# Revit family: NBS_DudleyIndustriesLimited_HndDriers_PlatinumRangeHandDryer
name_source: partatom
category: Specialty Equipment
revit_build: Autodesk Revit 2018 (Build: 20190510_1515(x64)
units: mm (PartAtom-declared; Revit-internal decimal feet)

## family parameters
Cut with Voids When Loaded = No
Host = Face
Part Type = Normal
Room Calculation Point = No
Round Connector Dimension = Use Diameter
Shared = No

## types (1)
- PlatinumRangeHandDryer
    ApparentLoad = 0 VA
    AssetType = Fixed
    BIMObjectName = NBS_DudleyIndustriesLimited_HandDryers_PlatinumRangeHandDryer
    BodyDimensions = 220 x 340 x 170 mm
    BodyFinish = Brushed with clear lacquer
    BodyMaterial = Stainless steel
    Category = Pr_40_70_62_37:Hand dryers
    CodePerformance = CE approved
    Default Elevation = 1300 mm  [stored 4.26509 ft]
    Depth = 0 mm  [stored 0 ft]
    Description = Platinum range hand dryer
    DurationUnit = year
    ElectricalSupplyPowerRating = 1.7 kW
    Features = High performance, robust and reliable, comfortable and quick
    Finish = Brushed with clear lacquer
    HandDryerMaterial = NBS_DudleyIndustriesLimited_StainlessSteel_Brushed
    HasProtectiveEarth = No
    IfcExportAs = IfcElectricApplianceType
    IfcExportType = HANDDRYER
    LoadClassification = Other
    ManufacturerName = Dudley Industries Limited
    ManufacturerURL = www.dudleyindustries.com
    Material = Stainless steel
    ModelNumber = 38155CB
    ModelReference = PlatinumRangeHandDryer
    NBSCertification = www.nationalbimlibrary.com/cert/3l0v0uwc
    NBSDescription = Hand dryers
    NBSReference = 45-35-72/334
    Name = HandDryers_PlatinumRangeHandDryer_DudleyIndustriesLimited
    NominalHeight = 340 mm
    NominalLength = 0 mm  [stored 0 ft]
    NominalWidth = 220 mm
    NumberOfPoles = 0
    Operation = Hand sensor
    PowerFactor = 0
    ProductInformation = https://www.dudleyindustries.com
    Shape = Rectangular
    Size = 340 x 220 x 170 mm
    Status = UNSET
    Uniclass2015Code = Pr_40_70_62_37
    Uniclass2015Title = Hand dryers
    Uniclass2015Version = Products v1.18
    Version = 1
    Voltage = 0 V
    WarrantyDescription = 5 Years
    WarrantyDurationUnit = year
    Weight = 7.14 kg

note: [stored X ft] marks values corroborated as IEEE doubles in the binary element streams (Revit-internal decimal feet)

## geometry (parser evidence)
native form markers: Sweep x2
no freeform markers — native parametric forms only
